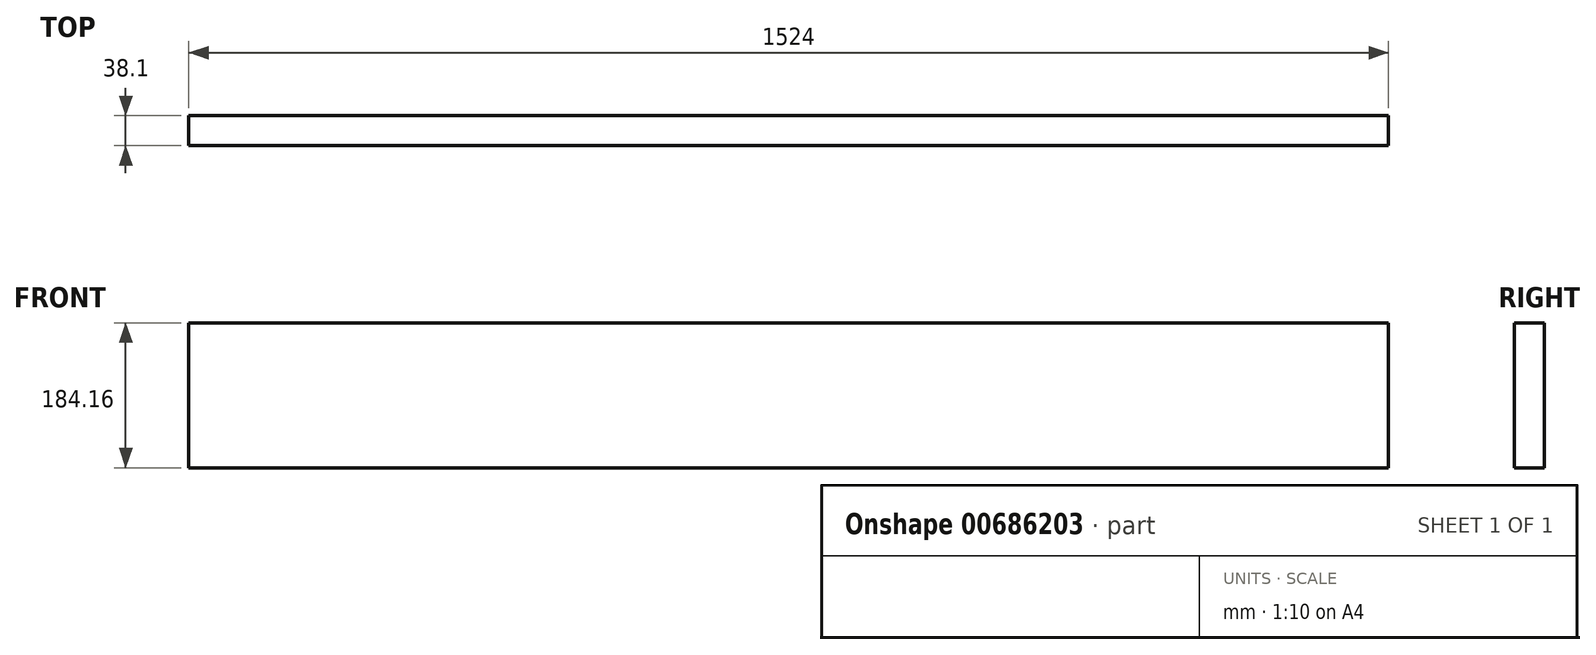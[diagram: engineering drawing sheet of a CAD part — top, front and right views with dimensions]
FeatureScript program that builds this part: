
annotation { "Feature Type Name" : "Feature", "Feature Type Description" : "" }
export const myFeature = defineFeature(function(context is Context, id is Id, definition is map)
    precondition{}
    {
        {
            var Q0;
            Q0=qCreatedBy(makeId("Front.planeOp"),FACE);
            var sketch = newSketch(context, id + "F0", { "sketchPlane" : qUnion([Q0])});
            skLineSegment(sketch, "E0.bottom", {"start": v(-762, 92.08) * mm, "end": v(762, 92.08) * mm});
            skLineSegment(sketch, "E0.top", {"start": v(-762, -92.08) * mm, "end": v(762, -92.08) * mm});
            skLineSegment(sketch, "E0.left", {"start": v(-762, 92.08) * mm, "end": v(-762, -92.08) * mm});
            skLineSegment(sketch, "E0.right", {"start": v(762, 92.08) * mm, "end": v(762, -92.08) * mm});
            skPoint(sketch, "E0.middle", {"position": v(0, 0) * mm});
            skSolve(sketch);
        }
        {
            var Q0;
            Q0 = qSketchRegion(id + "F0", true);
            extrude(context, id + "F1", {"entities" : qUnion([Q0]), "depth" : 38.1 * mm, "offsetDistance" : 25.4 * mm});
        }
    });
